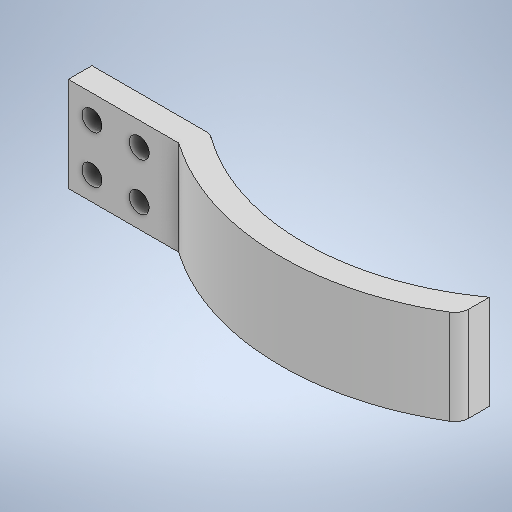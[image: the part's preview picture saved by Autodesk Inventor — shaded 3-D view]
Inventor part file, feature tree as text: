
AUTODESK INVENTOR PART (.ipt)
format: ipt  version: 2025.1 (Build 291241000, 241)  size: 270,336 bytes
history: native  units: mm
features: sketch x3, extrude x2, fillet x2, projected_geometry x1
ambient origin geometry x8: Origin, YZ Plane, XZ Plane, XY Plane, X Axis, Y Axis, Z Axis, Center Point
bodies: Solid1 (feature_tree)
feature tree (8):
  extrude  "Extrusion1"  Depth=25.0mm
  extrude  "Extrusion2"  Depth=4.999995mm
  fillet  "Fillet1"  Radius=20.0mm
  fillet  "Fillet2"  Radius=4.2mm
  sketch  "Sketch1"  dims[d0=60.0mm d1=25.0mm]
  sketch  "Sketch2"  dims[d9=20.0mm d11=10.0mm d12=20.0mm d14=10.0mm d17=10.0mm d18=5.0mm d19=20.0mm d20=0.0mm d21=3.0mm d22=2.5mm]
  projected_geometry  "Projected Loop1"
  sketch  "Sketch Rectangular Pattern1"  dims[d2=100.0mm d5=4.999995mm d6=20.0mm d7=0.0mm d8=4.2mm]
